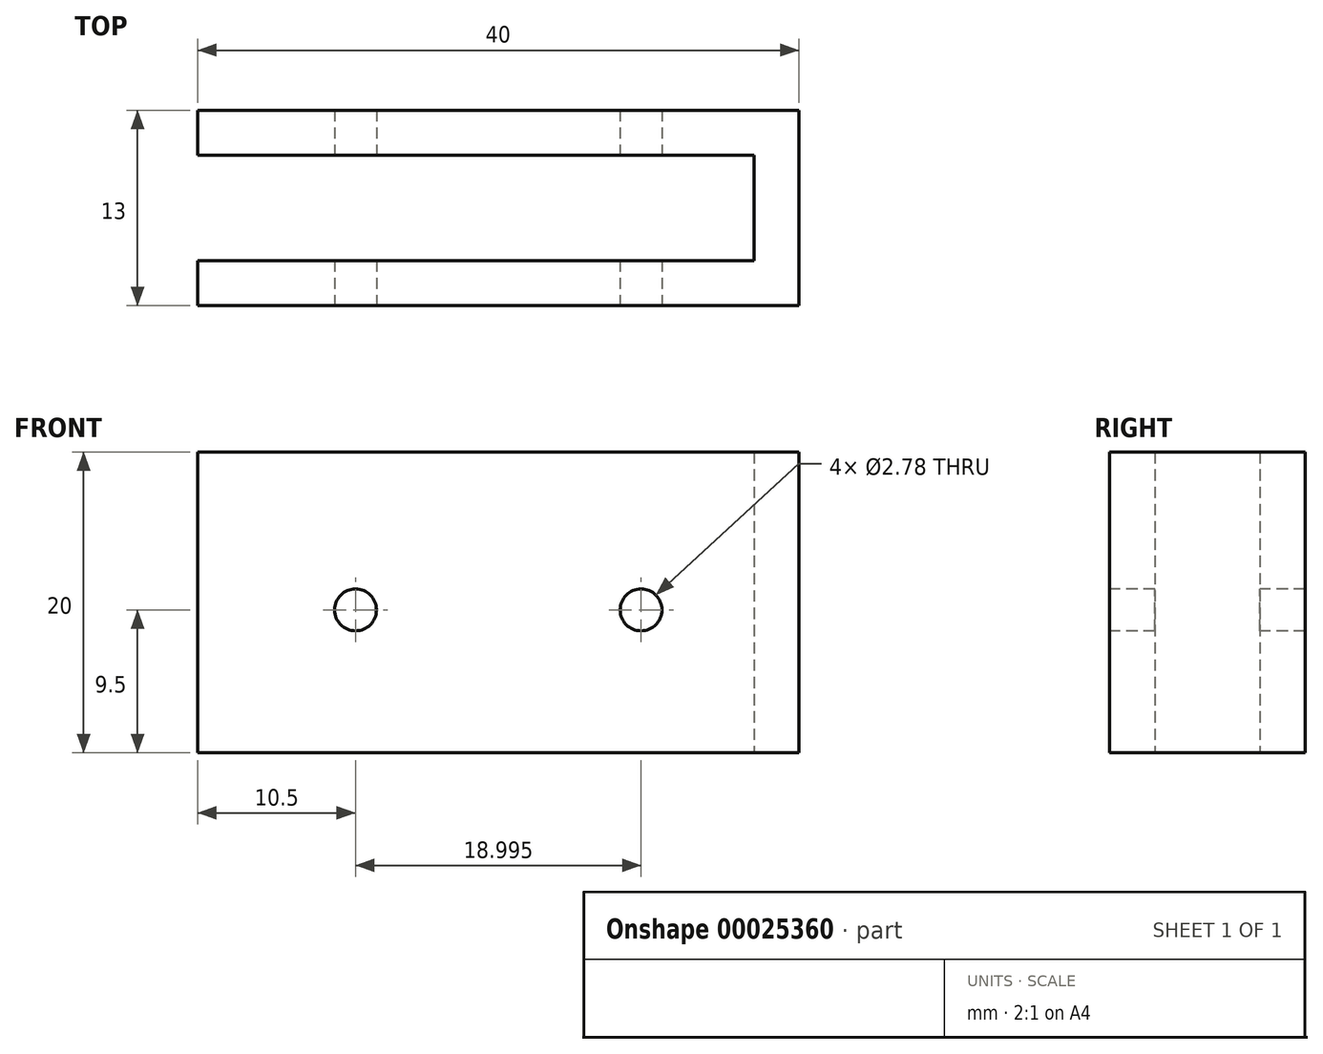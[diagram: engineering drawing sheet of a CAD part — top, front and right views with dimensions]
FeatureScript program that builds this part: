
annotation { "Feature Type Name" : "Feature", "Feature Type Description" : "" }
export const myFeature = defineFeature(function(context is Context, id is Id, definition is map)
    precondition{}
    {
        {
            var Q0;
            Q0=qCreatedBy(makeId("Front.planeOp"),FACE);
            var sketch = newSketch(context, id + "F0", { "sketchPlane" : qUnion([Q0])});
            skLineSegment(sketch, "E0.rect.bottom", {"start": v(-20, 10) * mm, "end": v(20, 10) * mm});
            skLineSegment(sketch, "E0.rect.top", {"start": v(-20, -10) * mm, "end": v(20, -10) * mm});
            skLineSegment(sketch, "E0.rect.left", {"start": v(-20, 10) * mm, "end": v(-20, -10) * mm});
            skLineSegment(sketch, "E0.rect.right", {"start": v(20, 10) * mm, "end": v(20, -10) * mm});
            skPoint(sketch, "E0.rect.middle", {"position": v(0, 0) * mm});
            skSolve(sketch);
        }
        {
            var Q0;
            Q0 = qSketchRegion(id + "F0", true);
            extrude(context, id + "F1", {"entities" : qUnion([Q0]), "depth" : 3 * mm});
        }
        {
            var Q0;
            Q0=makeQuery(id+"F1.opExtrude","CAP_FACE",FACE,{"disambiguationData":[OSD([sQuery(id+"F0.wireOp",EDGE,"E0.rect.bottom"),sQuery(id+"F0.wireOp",EDGE,"E0.rect.top"),sQuery(id+"F0.wireOp",EDGE,"E0.rect.left"),sQuery(id+"F0.wireOp",EDGE,"E0.rect.right")])],"isStart":false});
            var sketch = newSketch(context, id + "F2", { "sketchPlane" : qUnion([Q0])});
            skLineSegment(sketch, "E1.bottom", {"start": v(20, 10) * mm, "end": v(17, 10) * mm});
            skLineSegment(sketch, "E1.top", {"start": v(20, -10) * mm, "end": v(17, -10) * mm});
            skLineSegment(sketch, "E1.left", {"start": v(20, 10) * mm, "end": v(20, -10) * mm});
            skLineSegment(sketch, "E1.right", {"start": v(17, 10) * mm, "end": v(17, -10) * mm});
            skSolve(sketch);
        }
        {
            var Q0;
            Q0 = qSketchRegion(id + "F2", true);
            extrude(context, id + "F3", {"entities" : qUnion([Q0]), "operationType" : NewBodyOperationType.ADD, "depth" : 7 * mm});
        }
        {
            var Q0;
            Q0=makeQuery(id+"F3.opExtrude","CAP_FACE",FACE,{"disambiguationData":[OSD([sQuery(id+"F2.wireOp",EDGE,"E1.bottom"),sQuery(id+"F2.wireOp",EDGE,"E1.top"),sQuery(id+"F2.wireOp",EDGE,"E1.left"),sQuery(id+"F2.wireOp",EDGE,"E1.right")])],"isStart":false});
            var sketch = newSketch(context, id + "F4", { "sketchPlane" : qUnion([Q0])});
            skLineSegment(sketch, "E2.bottom", {"start": v(20, -10) * mm, "end": v(-20, -10) * mm});
            skLineSegment(sketch, "E2.top", {"start": v(20, 10) * mm, "end": v(-20, 10) * mm});
            skLineSegment(sketch, "E2.left", {"start": v(20, -10) * mm, "end": v(20, 10) * mm});
            skLineSegment(sketch, "E2.right", {"start": v(-20, -10) * mm, "end": v(-20, 10) * mm});
            skSolve(sketch);
        }
        {
            var Q0;
            Q0 = qSketchRegion(id + "F4", true);
            extrude(context, id + "F5", {"entities" : qUnion([Q0]), "operationType" : NewBodyOperationType.ADD, "depth" : 3 * mm});
        }
        {
            var Q0;
            Q0=makeQuery(id+"F5.opExtrude","CAP_FACE",FACE,{"disambiguationData":[OSD([sQuery(id+"F4.wireOp",EDGE,"E2.bottom"),sQuery(id+"F4.wireOp",EDGE,"E2.top"),sQuery(id+"F4.wireOp",EDGE,"E2.left"),sQuery(id+"F4.wireOp",EDGE,"E2.right")])],"isStart":false});
            var sketch = newSketch(context, id + "F6", { "sketchPlane" : qUnion([Q0])});
            skLineSegment(sketch, "E3.bottom", {"start": v(-20, 10) * mm, "end": v(-9.5, 10) * mm, "construction": true});
            skLineSegment(sketch, "E3.top", {"start": v(-20, -0.5) * mm, "end": v(-9.5, -0.5) * mm, "construction": true});
            skLineSegment(sketch, "E3.left", {"start": v(-20, 10) * mm, "end": v(-20, -0.5) * mm, "construction": true});
            skLineSegment(sketch, "E3.right", {"start": v(-9.5, 10) * mm, "end": v(-9.5, -0.5) * mm, "construction": true});
            skCircle(sketch, "E4", {"center": v(-9.5, -0.5) * mm, "radius": 1.39 * mm});
            skLineSegment(sketch, "E5", {"start": v(-9.5, -0.5) * mm, "end": v(9.5, -0.5) * mm, "construction": true});
            skCircle(sketch, "E6", {"center": v(9.5, -0.5) * mm, "radius": 1.39 * mm});
            skSolve(sketch);
        }
        {
            var Q0;
            Q0 = qSketchRegion(id + "F6", true);
            extrude(context, id + "F7", {"entities" : qUnion([Q0]), "operationType" : NewBodyOperationType.REMOVE, "oppositeDirection" : true, "depth" : 25 * mm});
        }
    });
